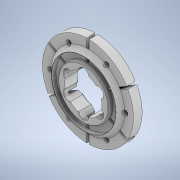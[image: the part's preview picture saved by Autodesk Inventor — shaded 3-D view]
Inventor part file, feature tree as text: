
AUTODESK INVENTOR PART (.ipt)
format: ipt  version: 2020 (Build 240168000, 168)  size: 5,182,464 bytes
history: native  units: in
note: dims shown in document units (in); Inventor stores cm internally (conversion verified against a paired STEP export)
features: extrude x6, sketch x6, other x4, chamfer x3, reference x2, imported_body x1, boolean_combine x1, pattern_circular x1, fillet x1, projected_geometry x1
ambient origin geometry x8: Origin, YZ Plane, XZ Plane, XY Plane, X Axis, Y Axis, Z Axis, Center Point
bodies: Solid1 (feature_tree), Solid2 (feature_tree)
feature tree (26):
  extrude  "Extrusion1"  Depth=0.477in
  imported_body  "Base1"
  boolean_combine  "Combine1"
  extrude  "Extrusion2"  Depth=2.74in
  extrude  "Extrusion3"  Depth=0.55in
  chamfer  "Chamfer1"  Distance=0.25in
  chamfer  "Chamfer2"  Distance=0.25in Angle=45.0deg
  extrude  "Extrusion4"  Depth=0.05in
  extrude  "Extrusion5"  Depth=0.05in TaperAngle=360.0deg
  chamfer  "Chamfer3"  [1 undecoded]
  extrude  "Extrusion6"  Depth=0.05in
  pattern_circular  "Circular Pattern1"  [2 undecoded]
  fillet  "Fillet1"  Radius=0.05in
  sketch  "Sketch1"  dims[d0=0.477in d1=0.0in d4=1.95in]
  reference  "Reference1"
  sketch  "Sketch3"  dims[d5=0.0in d6=0.0in d7=2.74in]
  sketch  "Sketch4"  dims[d8=0.4375in d9=0.55in d10=0.25in d11=0.0in]
  projected_geometry  "Projected Loop1"
  sketch  "Sketch6"  dims[d12=3.51in]
  reference  "Reference2"
  sketch  "Sketch7"  dims[d13=4.01in d14=0.25in d15=0.125in d16=45.0deg]
  sketch  "Sketch8"  dims[d17=0.025in d18=0.125in d19=45.0deg d20=0.2656in d21=2.3622in d23=360.0deg d25=0.0in d26=0.0in d27=2.0357in d28=0.0in d29=0.0in d30=0.05in d31=0.125in d32=45.0deg d33=0.0079in d34=0.0079in d35=2.485in d36=0.0in d37=2.3622in d38=360.0deg d40=0.05in d3=0.5in]
  other  "<userpath>\Documents\FRC\2020\Shooter\WheelAndFlywheel2.iam"
  other  "WheelAndFlywheel2.iam"
  other  "6 wheel Rev 4:1"
  other  "TopFlywheelClamp2:1"
note: 3 required parameter values undecoded (feature->parameter linkage not recoverable at this tier; creation-order binding heuristic only, values carry confidence <= 0.55)
